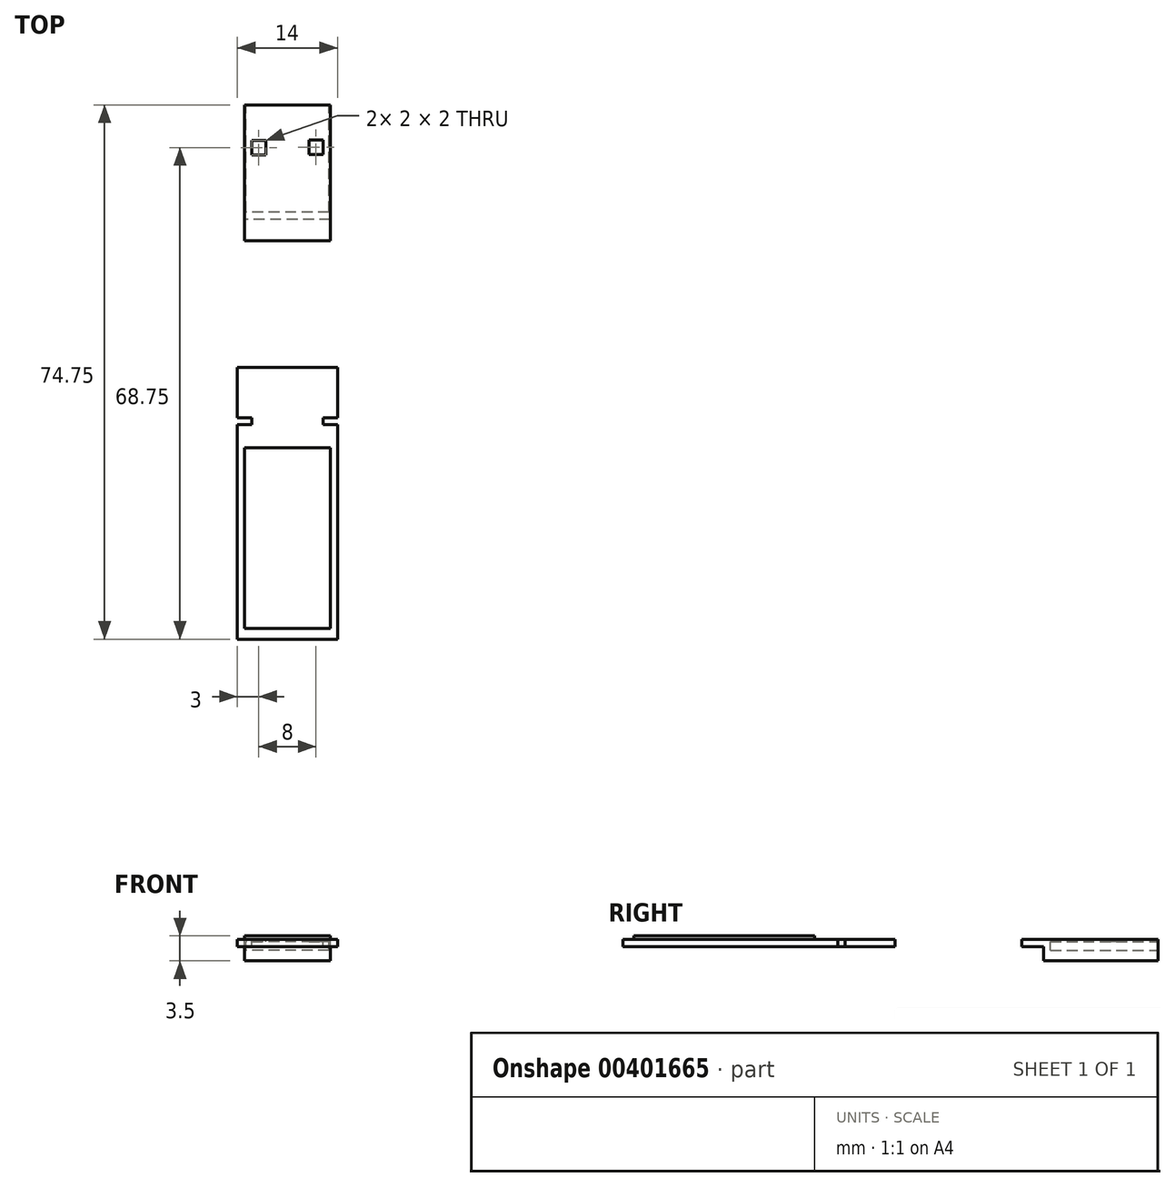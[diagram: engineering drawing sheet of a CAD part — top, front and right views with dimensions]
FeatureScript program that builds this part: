
annotation { "Feature Type Name" : "Feature", "Feature Type Description" : "" }
export const myFeature = defineFeature(function(context is Context, id is Id, definition is map)
    precondition{}
    {
        {
            var Q0;
            Q0=qCreatedBy(makeId("Top.planeOp"),FACE);
            var sketch = newSketch(context, id + "F0", { "sketchPlane" : qUnion([Q0])});
            skLineSegment(sketch, "E0.bottom", {"start": v(-6, 9.5) * mm, "end": v(6, 9.5) * mm});
            skLineSegment(sketch, "E0.top", {"start": v(-6, -9.5) * mm, "end": v(6, -9.5) * mm});
            skLineSegment(sketch, "E0.left", {"start": v(-6, 9.5) * mm, "end": v(-6, -9.5) * mm});
            skLineSegment(sketch, "E0.right", {"start": v(6, 9.5) * mm, "end": v(6, -9.5) * mm});
            skSolve(sketch);
        }
        {
            var Q0;
            Q0=qCreatedBy(makeId("Right.planeOp"),FACE);
            var sketch = newSketch(context, id + "F1", { "sketchPlane" : qUnion([Q0])});
            skLineSegment(sketch, "E1.0", {"start": v(9.5, 0) * mm, "end": v(-9.5, 0) * mm});
            skLineSegment(sketch, "E2", {"start": v(9.5, 0) * mm, "end": v(9.5, -3) * mm});
            skLineSegment(sketch, "E3", {"start": v(9.5, -3) * mm, "end": v(-6.5, -3) * mm});
            skLineSegment(sketch, "E4", {"start": v(-6.5, -3) * mm, "end": v(-6.5, -1) * mm});
            skLineSegment(sketch, "E5", {"start": v(-6.5, -1) * mm, "end": v(-9.5, -1) * mm});
            skLineSegment(sketch, "E6", {"start": v(-9.5, -1) * mm, "end": v(-9.5, 0) * mm});
            skSolve(sketch);
        }
        {
            var Q0;
            Q0=makeQuery(id+"F1.imprint","IMPRINT",FACE,{"disambiguationData":[TD([[makeQuery(id+"F1.imprint","IMPRINT",EDGE,{"derivedFrom":sQuery(id+"F1.wireOp",EDGE,"E1.0")}),1.0]])]});
            extrude(context, id + "F2", {"entities" : qUnion([Q0]), "endBound" : BoundingType.SYMMETRIC, "depth" : 12 * mm});
        }
        {
            var Q0;
            Q0=qCreatedBy(makeId("Top.planeOp"),FACE);
            var sketch = newSketch(context, id + "F3", { "sketchPlane" : qUnion([Q0])});
            skLineSegment(sketch, "E7", {"start": v(0, -24.42) * mm, "end": v(0, -66.64) * mm, "construction": true});
            skLineSegment(sketch, "E8", {"start": v(-10.15, -46.25) * mm, "end": v(10.92, -46.25) * mm, "construction": true});
            skLineSegment(sketch, "E9.bottom", {"start": v(-7, -27.25) * mm, "end": v(7, -27.25) * mm});
            skLineSegment(sketch, "E9.top", {"start": v(-7, -65.25) * mm, "end": v(7, -65.25) * mm});
            skLineSegment(sketch, "E9.left", {"start": v(-7, -27.25) * mm, "end": v(-7, -34.25) * mm});
            skLineSegment(sketch, "E9.right", {"start": v(7, -27.25) * mm, "end": v(7, -34.25) * mm});
            skLineSegment(sketch, "E10", {"start": v(7, -34.25) * mm, "end": v(5, -34.25) * mm});
            skLineSegment(sketch, "E11", {"start": v(5, -34.25) * mm, "end": v(5, -35.25) * mm});
            skLineSegment(sketch, "E12", {"start": v(-5, -35.25) * mm, "end": v(-5, -34.25) * mm});
            skLineSegment(sketch, "E13", {"start": v(-5, -34.25) * mm, "end": v(-7, -34.25) * mm});
            skLineSegment(sketch, "E14", {"start": v(-7, -34.25) * mm, "end": v(-7, -27.25) * mm});
            skLineSegment(sketch, "E15", {"start": v(-5, -35.25) * mm, "end": v(-7, -35.25) * mm});
            skLineSegment(sketch, "E16", {"start": v(5, -35.25) * mm, "end": v(7, -35.25) * mm});
            skLineSegment(sketch, "E17.trimOffspring", {"start": v(-7, -35.25) * mm, "end": v(-7, -65.25) * mm});
            skLineSegment(sketch, "E18.trimOffspring", {"start": v(7, -35.25) * mm, "end": v(7, -65.25) * mm});
            skSolve(sketch);
        }
        {
            var Q0;
            Q0=makeQuery(id+"F3.imprint","IMPRINT",FACE,{"disambiguationData":[TD([[makeQuery(id+"F3.imprint","IMPRINT",EDGE,{"derivedFrom":sQuery(id+"F3.wireOp",EDGE,"E9.bottom")}),-1.0]])]});
            extrude(context, id + "F4", {"entities" : qUnion([Q0]), "oppositeDirection" : true, "depth" : 1 * mm});
        }
        {
            var Q0;
            Q0=makeQuery(id+"F0.imprint","IMPRINT",FACE,{"disambiguationData":[TD([[makeQuery(id+"F0.imprint","IMPRINT",EDGE,{"derivedFrom":sQuery(id+"F0.wireOp",EDGE,"E0.bottom")}),-1.0]])]});
            cPlane(context, id + "F5", {"entities" : qUnion([Q0]), "cplaneType" : CPlaneType.OFFSET, "offset" : 0 * mm, "width" : 150 * mm, "height" : 150 * mm});
        }
        {
            var Q0;
            Q0=qCreatedBy(id+"F5.planeOp",FACE);
            var sketch = newSketch(context, id + "F6", { "sketchPlane" : qUnion([Q0])});
            skLineSegment(sketch, "E19.bottom", {"start": v(-5, 4.5) * mm, "end": v(-3, 4.5) * mm});
            skLineSegment(sketch, "E19.top", {"start": v(-5, 2.5) * mm, "end": v(-3, 2.5) * mm});
            skLineSegment(sketch, "E19.left", {"start": v(-5, 4.5) * mm, "end": v(-5, 2.5) * mm});
            skLineSegment(sketch, "E19.right", {"start": v(-3, 4.5) * mm, "end": v(-3, 2.5) * mm});
            skLineSegment(sketch, "E20.bottom", {"start": v(3, 4.57) * mm, "end": v(5, 4.57) * mm});
            skLineSegment(sketch, "E20.top", {"start": v(3, 2.57) * mm, "end": v(5, 2.57) * mm});
            skLineSegment(sketch, "E20.left", {"start": v(3, 4.57) * mm, "end": v(3, 2.57) * mm});
            skLineSegment(sketch, "E20.right", {"start": v(5, 4.57) * mm, "end": v(5, 2.57) * mm});
            skSolve(sketch);
        }
        {
            var Q0;
            Q0 = qSketchRegion(id + "F6", true);
            extrude(context, id + "F7", {"entities" : qUnion([Q0]), "operationType" : NewBodyOperationType.REMOVE, "oppositeDirection" : true, "depth" : 1 * mm});
        }
        {
            var Q0;
            Q0=makeQuery(id+"F2.opExtrude","SWEPT_FACE",FACE,{"disambiguationData":[OSD([sQuery(id+"F1.wireOp",EDGE,"E2")])]});
            cPlane(context, id + "F8", {"entities" : qUnion([Q0]), "cplaneType" : CPlaneType.OFFSET, "offset" : 0 * mm, "width" : 150 * mm, "height" : 150 * mm});
        }
        {
            var Q0;
            Q0=qCreatedBy(id+"F8.planeOp",FACE);
            var sketch = newSketch(context, id + "F9", { "sketchPlane" : qUnion([Q0])});
            skLineSegment(sketch, "E21.bottom", {"start": v(-5.8, -1.5) * mm, "end": v(5.8, -1.5) * mm});
            skLineSegment(sketch, "E21.top", {"start": v(-5.8, -0.3) * mm, "end": v(5.8, -0.3) * mm});
            skLineSegment(sketch, "E21.left", {"start": v(-5.8, -1.5) * mm, "end": v(-5.8, -0.3) * mm});
            skLineSegment(sketch, "E21.right", {"start": v(5.8, -1.5) * mm, "end": v(5.8, -0.3) * mm});
            skSolve(sketch);
        }
        {
            var Q0;
            Q0 = qSketchRegion(id + "F9", true);
            extrude(context, id + "F10", {"entities" : qUnion([Q0]), "operationType" : NewBodyOperationType.REMOVE, "oppositeDirection" : true, "depth" : 15 * mm});
        }
        {
            var Q0;
            Q0=makeQuery(id+"F4.opExtrude","CAP_FACE",FACE,{"disambiguationData":[OSD([sQuery(id+"F3.wireOp",EDGE,"E9.bottom"),sQuery(id+"F3.wireOp",EDGE,"E9.top"),sQuery(id+"F3.wireOp",EDGE,"E9.right"),sQuery(id+"F3.wireOp",EDGE,"E10"),sQuery(id+"F3.wireOp",EDGE,"E11"),sQuery(id+"F3.wireOp",EDGE,"E12"),sQuery(id+"F3.wireOp",EDGE,"E13"),sQuery(id+"F3.wireOp",EDGE,"E14"),sQuery(id+"F3.wireOp",EDGE,"E15"),sQuery(id+"F3.wireOp",EDGE,"E16"),sQuery(id+"F3.wireOp",EDGE,"E17.trimOffspring"),sQuery(id+"F3.wireOp",EDGE,"E18.trimOffspring")])],"isStart":true});
            cPlane(context, id + "F11", {"entities" : qUnion([Q0]), "cplaneType" : CPlaneType.OFFSET, "offset" : 0 * mm, "width" : 150 * mm, "height" : 150 * mm});
        }
        {
            var Q0;
            Q0=qCreatedBy(id+"F11.planeOp",FACE);
            var sketch = newSketch(context, id + "F12", { "sketchPlane" : qUnion([Q0])});
            skLineSegment(sketch, "E22.bottom", {"start": v(6, -38.48) * mm, "end": v(-6, -38.48) * mm});
            skLineSegment(sketch, "E22.top", {"start": v(6, -63.75) * mm, "end": v(-6, -63.75) * mm});
            skLineSegment(sketch, "E22.left", {"start": v(6, -38.48) * mm, "end": v(6, -63.75) * mm});
            skLineSegment(sketch, "E22.right", {"start": v(-6, -38.48) * mm, "end": v(-6, -63.75) * mm});
            skSolve(sketch);
        }
        {
            var Q0;
            Q0 = qSketchRegion(id + "F12", true);
            extrude(context, id + "F13", {"entities" : qUnion([Q0]), "operationType" : NewBodyOperationType.ADD, "depth" : .5 * mm});
        }
    });
